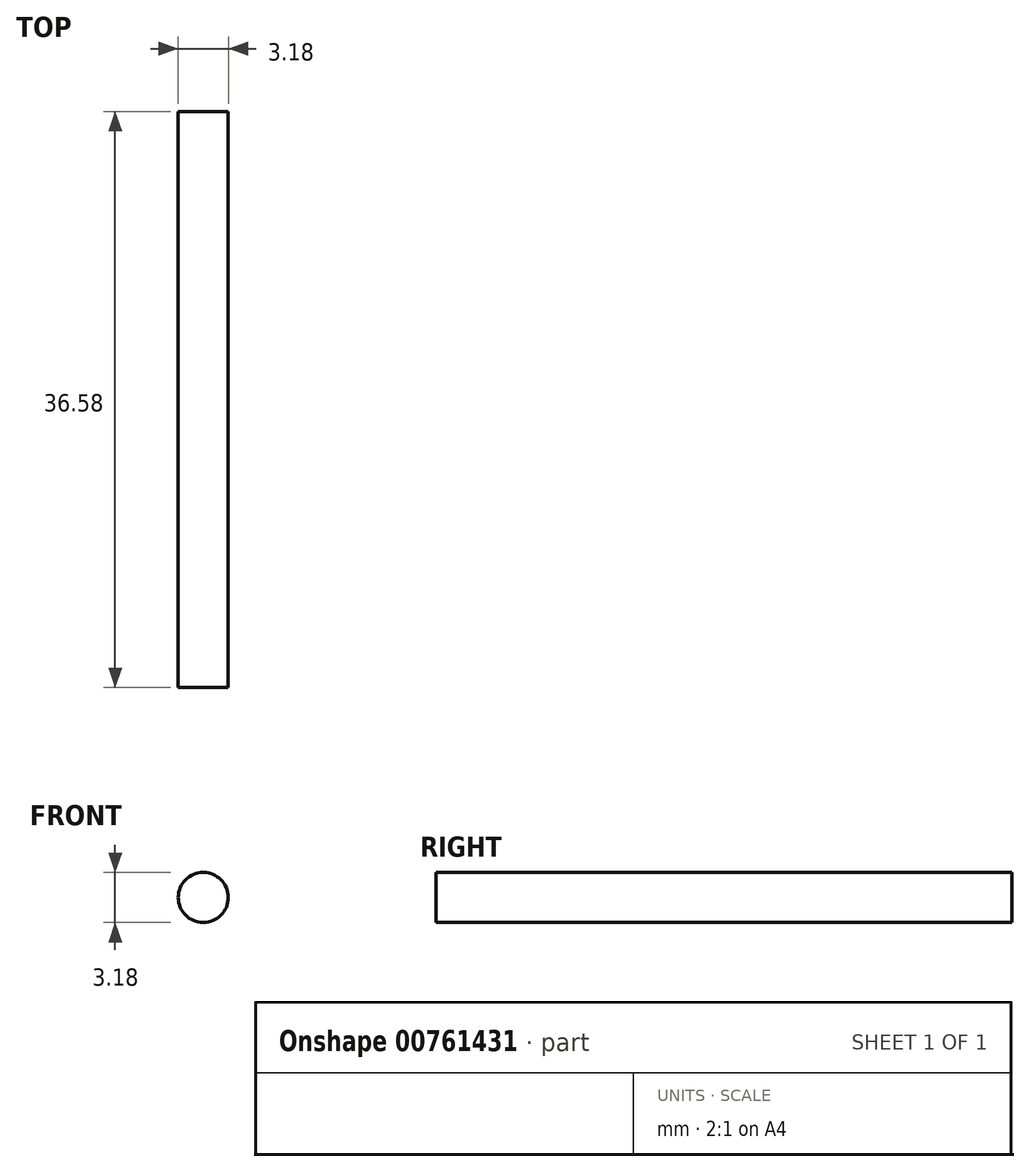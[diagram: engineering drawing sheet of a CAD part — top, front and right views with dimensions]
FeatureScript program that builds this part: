
annotation { "Feature Type Name" : "Feature", "Feature Type Description" : "" }
export const myFeature = defineFeature(function(context is Context, id is Id, definition is map)
    precondition{}
    {
        {
            var Q0;
            Q0=qCreatedBy(makeId("Front.planeOp"),FACE);
            var sketch = newSketch(context, id + "F0", { "sketchPlane" : qUnion([Q0])});
            skCircle(sketch, "E0", {"center": v(0, 0) * mm, "radius": 1.59 * mm});
            skSolve(sketch);
        }
        {
            var Q0;
            Q0 = qSketchRegion(id + "F0", true);
            extrude(context, id + "F1", {"entities" : qUnion([Q0]), "depth" : 36.58 * mm, "offsetDistance" : 25.4 * mm});
        }
    });
